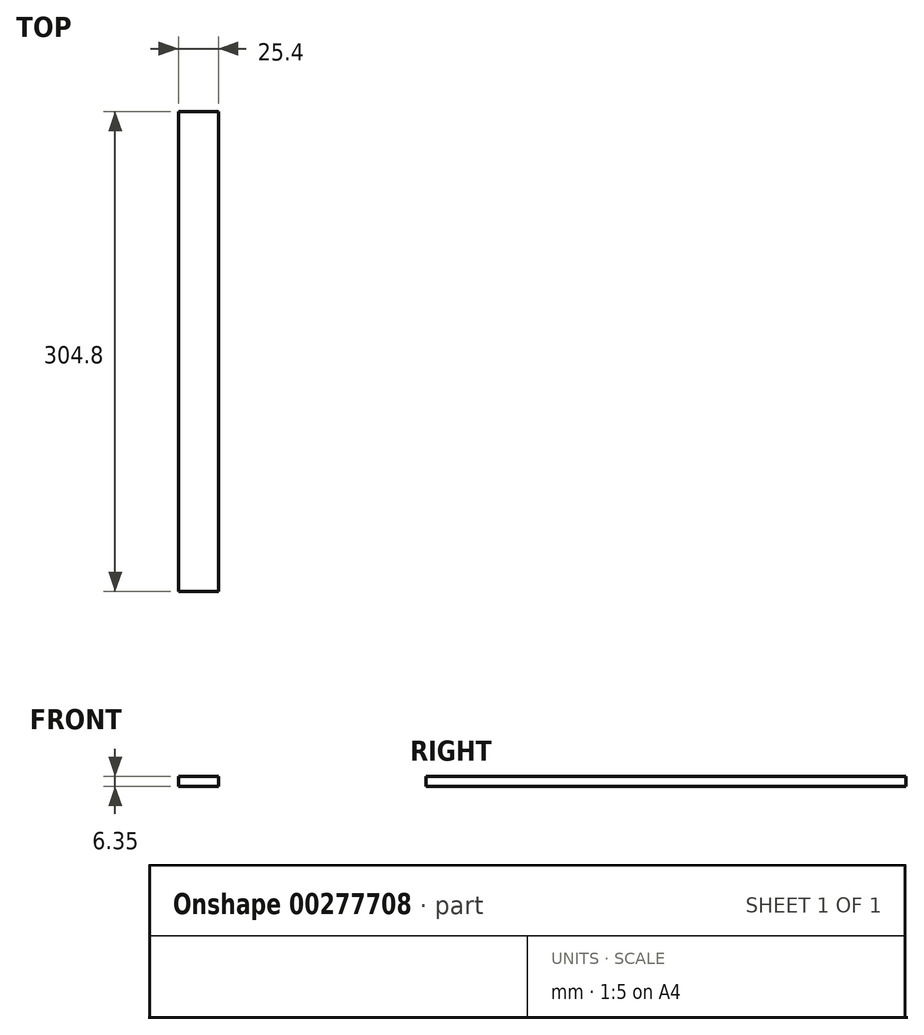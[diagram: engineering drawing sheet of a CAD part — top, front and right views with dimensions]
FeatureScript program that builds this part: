
annotation { "Feature Type Name" : "Feature", "Feature Type Description" : "" }
export const myFeature = defineFeature(function(context is Context, id is Id, definition is map)
    precondition{}
    {
        {
            var Q0;
            Q0=qCreatedBy(makeId("Top.planeOp"),FACE);
            var sketch = newSketch(context, id + "F0", { "sketchPlane" : qUnion([Q0])});
            skLineSegment(sketch, "E0.bottom", {"start": v(-20.32, 231.1) * mm, "end": v(5.08, 231.1) * mm});
            skLineSegment(sketch, "E0.top", {"start": v(-20.32, -73.7) * mm, "end": v(5.08, -73.7) * mm});
            skLineSegment(sketch, "E0.left", {"start": v(-20.32, 231.1) * mm, "end": v(-20.32, -73.7) * mm});
            skLineSegment(sketch, "E0.right", {"start": v(5.08, 231.1) * mm, "end": v(5.08, -73.7) * mm});
            skSolve(sketch);
        }
        {
            var Q0;
            Q0 = qSketchRegion(id + "F0", true);
            extrude(context, id + "F1", {"entities" : qUnion([Q0]), "depth" : 6.35 * mm});
        }
    });
